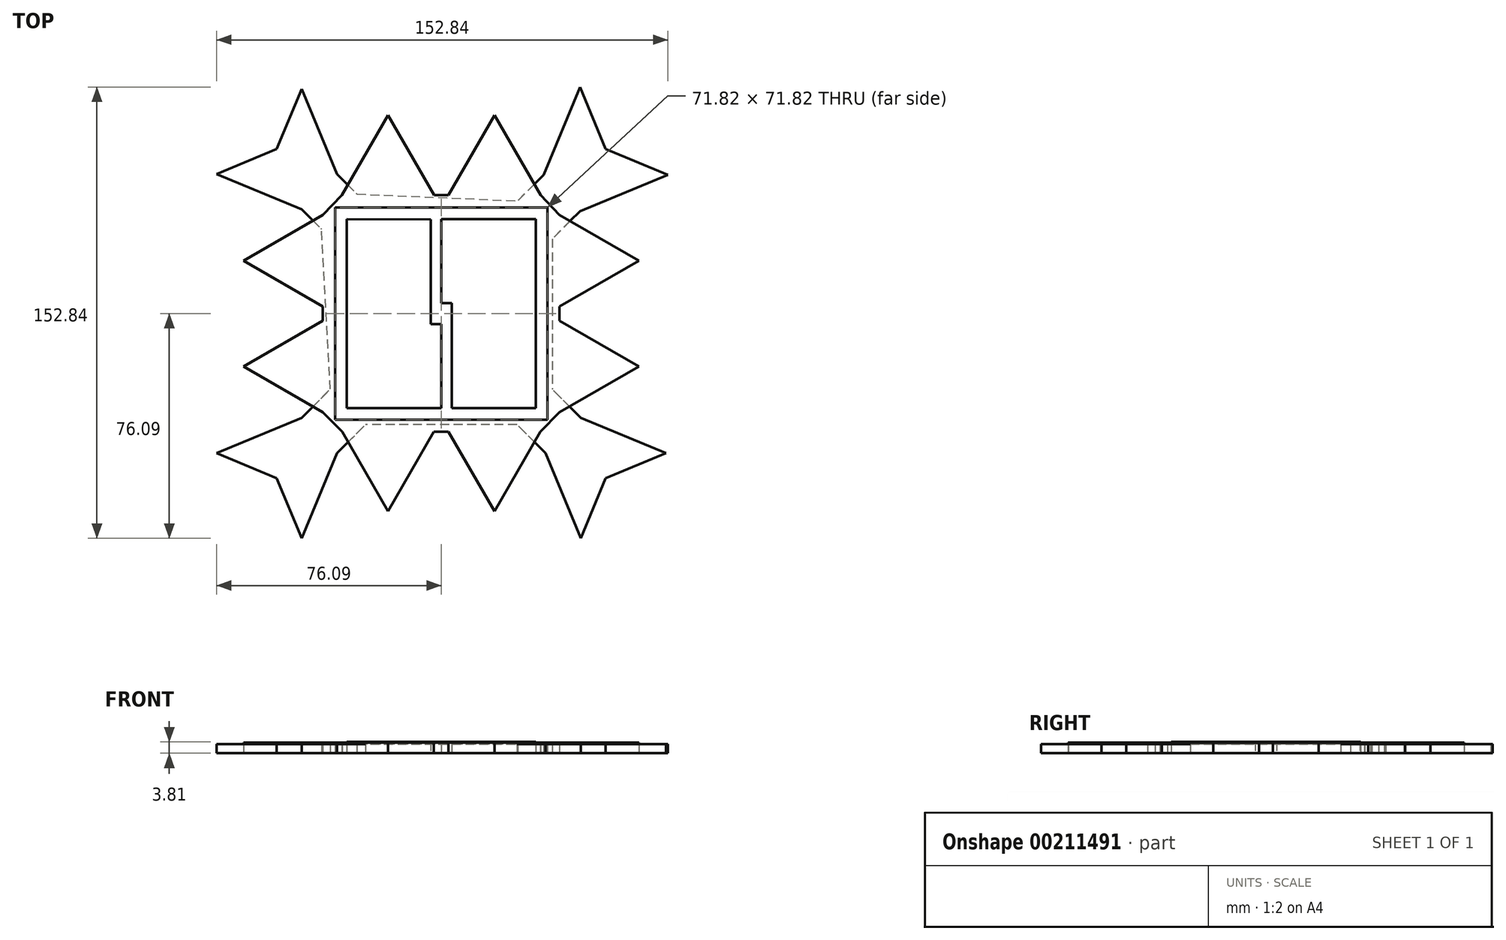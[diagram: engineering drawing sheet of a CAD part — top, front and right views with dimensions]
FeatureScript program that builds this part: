
annotation { "Feature Type Name" : "Feature", "Feature Type Description" : "" }
export const myFeature = defineFeature(function(context is Context, id is Id, definition is map)
    precondition{}
    {
        {
            var Q0;
            Q0=qCreatedBy(makeId("Top.planeOp"),FACE);
            var sketch = newSketch(context, id + "F0", { "sketchPlane" : qUnion([Q0])});
            skLineSegment(sketch, "E0.1", {"start": v(32.02, 32.02) * mm, "end": v(32.02, -32.02) * mm});
            skLineSegment(sketch, "E0.3", {"start": v(-32.02, -32.02) * mm, "end": v(-32.02, 32.02) * mm});
            skPoint(sketch, "E0.0.midPoint", {"position": v(0, 32.02) * mm});
            skLineSegment(sketch, "E1.1", {"start": v(3.58, 3.58) * mm, "end": v(3.58, -3.58) * mm});
            skLineSegment(sketch, "E1.3", {"start": v(-3.58, -3.58) * mm, "end": v(-3.58, 3.58) * mm});
            skPoint(sketch, "E1.0.midPoint", {"position": v(0, 3.58) * mm});
            skLineSegment(sketch, "E2", {"start": v(-3.58, 3.58) * mm, "end": v(-3.58, 31.82) * mm});
            skLineSegment(sketch, "E3", {"start": v(0, 3.58) * mm, "end": v(0, 32.02) * mm});
            skLineSegment(sketch, "E4", {"start": v(0, -3.58) * mm, "end": v(0, -32.02) * mm});
            skLineSegment(sketch, "E5", {"start": v(3.58, -3.58) * mm, "end": v(3.58, -32.02) * mm});
            skLineSegment(sketch, "E6", {"start": v(-3.58, -3.58) * mm, "end": v(0.51, -3.58) * mm});
            skLineSegment(sketch, "E7", {"start": v(0, 3.58) * mm, "end": v(3.58, 3.58) * mm});
            skLineSegment(sketch, "E8", {"start": v(-32.02, -32.02) * mm, "end": v(0, -32.02) * mm});
            skLineSegment(sketch, "E9", {"start": v(3.58, -32.02) * mm, "end": v(32.02, -32.02) * mm});
            skLineSegment(sketch, "E10", {"start": v(32.02, 32.02) * mm, "end": v(0, 32.02) * mm});
            skLineSegment(sketch, "E11", {"start": v(-3.58, 31.82) * mm, "end": v(-32.02, 32.02) * mm});
            skSolve(sketch);
        }
        {
            var Q0;
            Q0 = qSketchRegion(id + "F0", true);
            extrude(context, id + "F1", {"entities" : qUnion([Q0]), "depth" : 3.8 * mm});
        }
        {
            var Q0;
            Q0=qCreatedBy(makeId("Top.planeOp"),FACE);
            var sketch = newSketch(context, id + "F2", { "sketchPlane" : qUnion([Q0])});
            skPoint(sketch, "E12.0.midPoint", {"position": v(0, 35.91) * mm});
            skPoint(sketch, "E13.0.midPoint", {"position": v(0, 67.17) * mm});
            skPoint(sketch, "E14.cCircle.perimeterSnap0", {"position": v(35.91, 0) * mm});
            skPoint(sketch, "E14.0.midPoint", {"position": v(66.89, 0) * mm});
            skPoint(sketch, "E14.0.midPoint.positionSnap0", {"position": v(35.91, 0) * mm});
            skPoint(sketch, "E15.cCircle.perimeterSnap0", {"position": v(-35.91, 0) * mm});
            skPoint(sketch, "E15.0.midPoint", {"position": v(-66.92, 0) * mm});
            skPoint(sketch, "E15.0.midPoint.positionSnap0", {"position": v(-35.91, 0) * mm});
            skPoint(sketch, "E16.0.midPoint", {"position": v(0.02, -66.96) * mm});
            skPoint(sketch, "E17.0.midPoint", {"position": v(0, 40.07) * mm});
            skLineSegment(sketch, "E18", {"start": v(-2.47, -40.07) * mm, "end": v(2.47, -40.07) * mm});
            skLineSegment(sketch, "E19", {"start": v(40.07, 2.4) * mm, "end": v(40.07, -2.4) * mm});
            skLineSegment(sketch, "E20", {"start": v(-2.4, 40.07) * mm, "end": v(2.4, 40.07) * mm});
            skLineSegment(sketch, "E21", {"start": v(-40.07, -2.4) * mm, "end": v(-40.07, 2.4) * mm});
            skLineSegment(sketch, "E22", {"start": v(-66.92, 17.9) * mm, "end": v(-40.07, 2.4) * mm});
            skLineSegment(sketch, "E23", {"start": v(-40.07, -2.4) * mm, "end": v(-66.92, -17.9) * mm});
            skLineSegment(sketch, "E24", {"start": v(-17.98, -66.97) * mm, "end": v(-2.47, -40.07) * mm});
            skLineSegment(sketch, "E25", {"start": v(18.01, -66.94) * mm, "end": v(2.47, -40.07) * mm});
            skLineSegment(sketch, "E26", {"start": v(66.89, -17.88) * mm, "end": v(40.07, -2.4) * mm});
            skLineSegment(sketch, "E27", {"start": v(66.89, 17.88) * mm, "end": v(40.07, 2.4) * mm});
            skLineSegment(sketch, "E28", {"start": v(18.05, 67.17) * mm, "end": v(2.4, 40.07) * mm});
            skLineSegment(sketch, "E29", {"start": v(-18.05, 67.17) * mm, "end": v(-2.4, 40.07) * mm});
            skLineSegment(sketch, "E30", {"start": v(-33.46, -40.07) * mm, "end": v(-40.07, -33.4) * mm});
            skLineSegment(sketch, "E31", {"start": v(33.51, -40.07) * mm, "end": v(40.07, -33.37) * mm});
            skLineSegment(sketch, "E32", {"start": v(40.07, 33.37) * mm, "end": v(33.7, 40.07) * mm});
            skLineSegment(sketch, "E33", {"start": v(-33.7, 40.07) * mm, "end": v(-40.07, 33.4) * mm});
            skLineSegment(sketch, "E34", {"start": v(-66.92, 17.9) * mm, "end": v(-40.07, 33.4) * mm});
            skLineSegment(sketch, "E35", {"start": v(-33.7, 40.07) * mm, "end": v(-18.05, 67.17) * mm});
            skLineSegment(sketch, "E36", {"start": v(18.05, 67.17) * mm, "end": v(33.7, 40.07) * mm});
            skLineSegment(sketch, "E37", {"start": v(40.07, 33.37) * mm, "end": v(66.89, 17.88) * mm});
            skLineSegment(sketch, "E38", {"start": v(66.89, -17.88) * mm, "end": v(40.07, -33.37) * mm});
            skLineSegment(sketch, "E39", {"start": v(33.51, -40.07) * mm, "end": v(18.01, -66.94) * mm});
            skLineSegment(sketch, "E40", {"start": v(-17.98, -66.97) * mm, "end": v(-33.46, -40.07) * mm});
            skLineSegment(sketch, "E41", {"start": v(-40.07, -33.4) * mm, "end": v(-66.92, -17.9) * mm});
            skLineSegment(sketch, "E42.0", {"start": v(35.91, 35.91) * mm, "end": v(35.91, -35.91) * mm});
            skLineSegment(sketch, "E42.1", {"start": v(35.91, -35.91) * mm, "end": v(-35.91, -35.91) * mm});
            skLineSegment(sketch, "E42.2", {"start": v(-35.91, -35.91) * mm, "end": v(-35.91, 35.91) * mm});
            skLineSegment(sketch, "E42.3", {"start": v(-35.91, 35.91) * mm, "end": v(35.91, 35.91) * mm});
            skLineSegment(sketch, "E43", {"start": v(-36.76, -36.74) * mm, "end": v(-35.91, -35.91) * mm});
            skLineSegment(sketch, "E44", {"start": v(36.79, -36.72) * mm, "end": v(35.91, -35.91) * mm});
            skPoint(sketch, "E45.startSnap0", {"position": v(36.88, 36.72) * mm});
            skLineSegment(sketch, "E46", {"start": v(36.88, 36.72) * mm, "end": v(35.91, 35.91) * mm});
            skLineSegment(sketch, "E47", {"start": v(-36.88, 36.74) * mm, "end": v(-35.91, 35.91) * mm});
            skLineSegment(sketch, "E48", {"start": v(0, -35.91) * mm, "end": v(0, -40.07) * mm});
            skPoint(sketch, "E48.startSnap0", {"position": v(0, -40.07) * mm});
            skLineSegment(sketch, "E49", {"start": v(-35.91, 0) * mm, "end": v(-40.07, 0) * mm});
            skLineSegment(sketch, "E50", {"start": v(0, 35.91) * mm, "end": v(0, 40.07) * mm});
            skLineSegment(sketch, "E51", {"start": v(35.91, 0) * mm, "end": v(40.07, 0) * mm});
            skSolve(sketch);
        }
        {
            var Q0;
            Q0 = qSketchRegion(id + "F2", true);
            extrude(context, id + "F3", {"entities" : qUnion([Q0]), "depth" : 3.56 * mm});
        }
        {
            var Q0;
            Q0=qCreatedBy(makeId("Top.planeOp"),FACE);
            var sketch = newSketch(context, id + "F4", { "sketchPlane" : qUnion([Q0])});
            skPoint(sketch, "E52.0.midPoint", {"position": v(0, 76.09) * mm});
            skLineSegment(sketch, "E53.5", {"start": v(46.98, 34.65) * mm, "end": v(34.65, 46.98) * mm});
            skPoint(sketch, "E53.0.midPoint", {"position": v(55.7, 76.75) * mm});
            skLineSegment(sketch, "E54.5", {"start": v(35.31, -47.26) * mm, "end": v(47.26, -35.31) * mm});
            skLineSegment(sketch, "E55.5", {"start": v(-47.26, -35.31) * mm, "end": v(-35.31, -47.26) * mm});
            skPoint(sketch, "E55.0.midPoint", {"position": v(-55.7, -76.09) * mm});
            skLineSegment(sketch, "E56.3", {"start": v(-35.31, 47.26) * mm, "end": v(-47.26, 35.31) * mm});
            skPoint(sketch, "E56.0.midPoint", {"position": v(-55.7, 76.09) * mm});
            skLineSegment(sketch, "E57", {"start": v(34.65, 46.98) * mm, "end": v(46.98, 76.75) * mm});
            skLineSegment(sketch, "E58", {"start": v(55.7, 55.7) * mm, "end": v(46.98, 76.75) * mm});
            skLineSegment(sketch, "E59", {"start": v(55.7, 55.7) * mm, "end": v(76.75, 46.98) * mm});
            skLineSegment(sketch, "E60", {"start": v(46.98, 34.65) * mm, "end": v(76.75, 46.98) * mm});
            skLineSegment(sketch, "E61", {"start": v(76.09, -47.26) * mm, "end": v(55.7, -55.7) * mm});
            skLineSegment(sketch, "E62", {"start": v(47.26, -76.09) * mm, "end": v(55.7, -55.7) * mm});
            skLineSegment(sketch, "E63", {"start": v(47.26, -76.09) * mm, "end": v(35.31, -47.26) * mm});
            skLineSegment(sketch, "E64", {"start": v(47.26, -35.31) * mm, "end": v(76.09, -47.26) * mm});
            skLineSegment(sketch, "E65", {"start": v(-47.26, -76.09) * mm, "end": v(-55.7, -55.7) * mm});
            skLineSegment(sketch, "E66", {"start": v(-76.09, -47.26) * mm, "end": v(-55.7, -55.7) * mm});
            skLineSegment(sketch, "E67", {"start": v(-47.26, -76.09) * mm, "end": v(-35.31, -47.26) * mm});
            skLineSegment(sketch, "E68", {"start": v(-76.09, -47.26) * mm, "end": v(-47.26, -35.31) * mm});
            skLineSegment(sketch, "E69", {"start": v(-47.26, 76.09) * mm, "end": v(-55.7, 55.7) * mm});
            skLineSegment(sketch, "E70", {"start": v(-76.09, 47.26) * mm, "end": v(-55.7, 55.7) * mm});
            skLineSegment(sketch, "E71", {"start": v(-47.26, 76.09) * mm, "end": v(-35.31, 47.26) * mm});
            skLineSegment(sketch, "E72", {"start": v(-76.09, 47.26) * mm, "end": v(-47.26, 35.31) * mm});
            skLineSegment(sketch, "E73", {"start": v(37.58, 25.3) * mm, "end": v(37.58, -25.63) * mm});
            skLineSegment(sketch, "E74", {"start": v(25.63, -37.58) * mm, "end": v(-25.59, -37.58) * mm});
            skLineSegment(sketch, "E75", {"start": v(-37.58, -25.59) * mm, "end": v(-40.5, 28.57) * mm});
            skLineSegment(sketch, "E76", {"start": v(-28.57, 40.5) * mm, "end": v(25.87, 38.16) * mm});
            skLineSegment(sketch, "E77", {"start": v(-35.31, -47.26) * mm, "end": v(-25.59, -37.58) * mm});
            skLineSegment(sketch, "E78", {"start": v(-47.26, -35.31) * mm, "end": v(-37.58, -25.59) * mm});
            skLineSegment(sketch, "E79", {"start": v(-47.26, 35.31) * mm, "end": v(-40.5, 28.57) * mm});
            skLineSegment(sketch, "E80", {"start": v(-35.31, 47.26) * mm, "end": v(-28.57, 40.5) * mm});
            skLineSegment(sketch, "E81", {"start": v(34.65, 46.98) * mm, "end": v(25.87, 38.16) * mm});
            skLineSegment(sketch, "E82", {"start": v(46.98, 34.65) * mm, "end": v(37.58, 25.3) * mm});
            skLineSegment(sketch, "E83", {"start": v(47.26, -35.31) * mm, "end": v(37.58, -25.63) * mm});
            skLineSegment(sketch, "E84", {"start": v(35.31, -47.26) * mm, "end": v(25.63, -37.58) * mm});
            skSolve(sketch);
        }
        {
            var Q0;
            Q0 = qSketchRegion(id + "F4", true);
            extrude(context, id + "F5", {"entities" : qUnion([Q0]), "depth" : 3.05 * mm});
        }
    });
